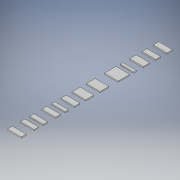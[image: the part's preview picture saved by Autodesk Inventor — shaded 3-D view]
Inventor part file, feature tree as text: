
AUTODESK INVENTOR PART (.ipt)
format: ipt  version: 2017 (Build 210142000, 142)  size: 163,840 bytes
history: native  units: in
note: dims shown in document units (in); Inventor stores cm internally (conversion verified against a paired STEP export)
features: extrude x1, sketch x1
ambient origin geometry x8: Origin, YZ Plane, XZ Plane, XY Plane, X Axis, Y Axis, Z Axis, Center Point
bodies: Solid1 (feature_tree)
feature tree (2):
  extrude  "Extrusion1"  Depth=0.9in
  sketch  "Sketch1"  dims[d0=2.5in d1=0.9in d2=0.8in d3=0.8in d4=2.5in d5=0.9in d6=0.6in d7=2.5in d8=1.0in d9=2.5in d10=1.5in d11=2.5in d12=1.6in d13=2.5in d14=2.1in d15=0.5in d16=1.2in d17=0.9in d18=2.5in d19=1.0in d20=0.2in d21=0.0in]
